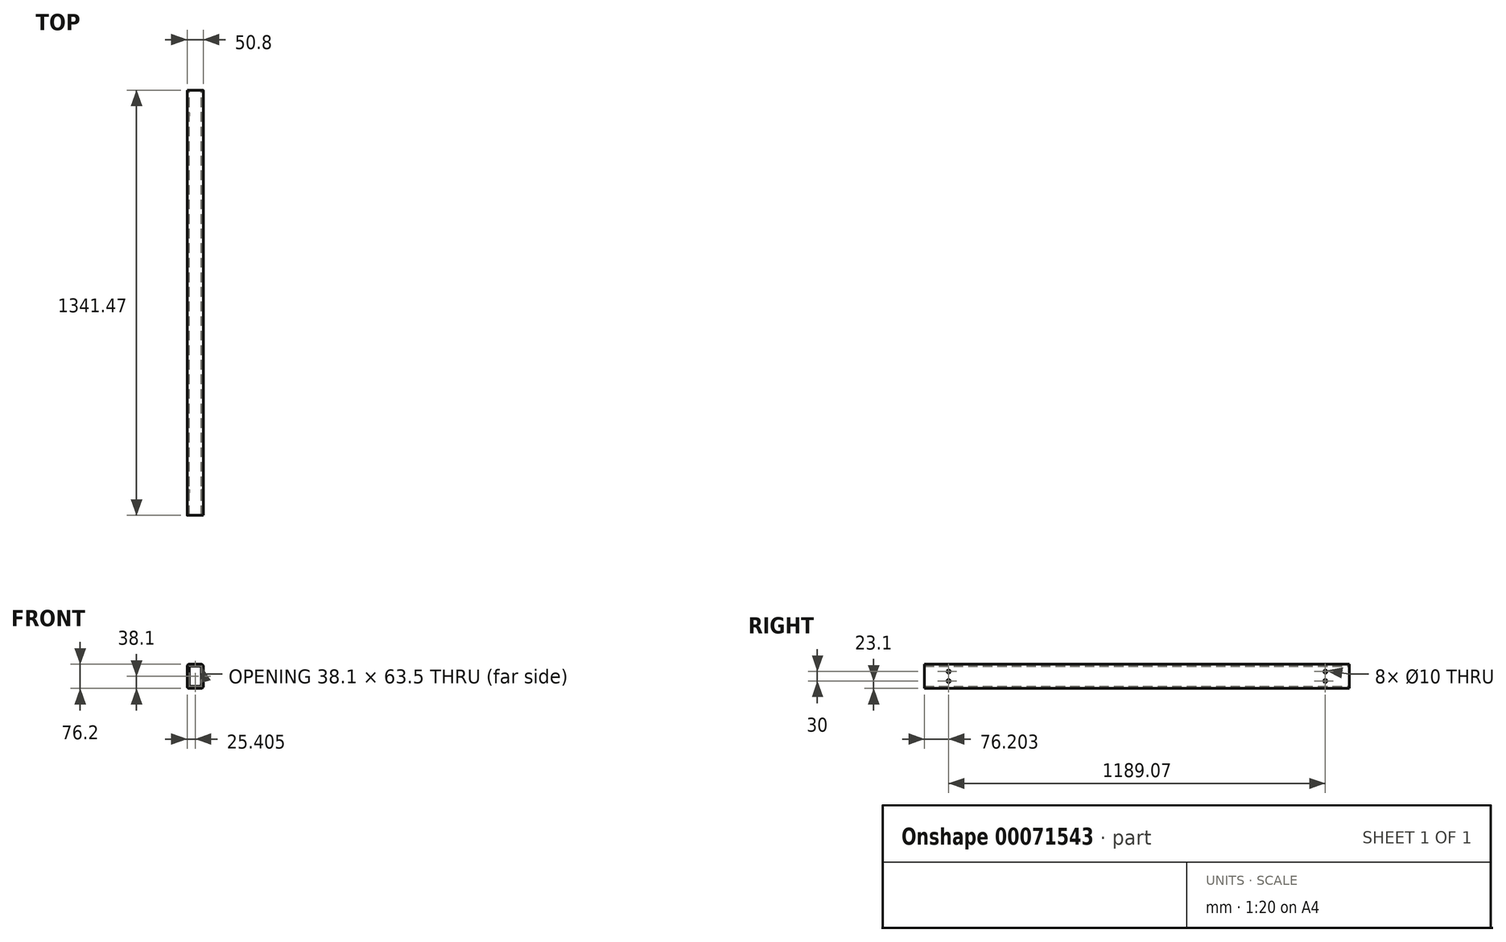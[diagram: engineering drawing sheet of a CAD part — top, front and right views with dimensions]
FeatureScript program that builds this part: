
annotation { "Feature Type Name" : "Feature", "Feature Type Description" : "" }
export const myFeature = defineFeature(function(context is Context, id is Id, definition is map)
    precondition{}
    {
        {
            var Q0;
            Q0=qCreatedBy(makeId("Front.planeOp"),FACE);
            var sketch = newSketch(context, id + "F0", { "sketchPlane" : qUnion([Q0])});
            skLineSegment(sketch, "E0.bottom", {"start": v(-40.1, 38.24) * mm, "end": v(-2, 38.24) * mm});
            skLineSegment(sketch, "E0.top", {"start": v(-40.1, -37.96) * mm, "end": v(-2, -37.96) * mm});
            skLineSegment(sketch, "E0.left", {"start": v(-46.45, 31.89) * mm, "end": v(-46.45, -31.61) * mm});
            skLineSegment(sketch, "E0.right", {"start": v(4.35, 31.89) * mm, "end": v(4.35, -31.61) * mm});
            skLineSegment(sketch, "E1.bottom", {"start": v(-33.75, 31.89) * mm, "end": v(-8.35, 31.89) * mm});
            skLineSegment(sketch, "E1.top", {"start": v(-33.75, -31.61) * mm, "end": v(-8.35, -31.61) * mm});
            skLineSegment(sketch, "E1.left", {"start": v(-40.1, 25.54) * mm, "end": v(-40.1, -25.26) * mm});
            skLineSegment(sketch, "E1.right", {"start": v(-2, 25.54) * mm, "end": v(-2, -25.26) * mm});
            skPoint(sketch, "E2.visualSharp", {"position": v(-40.1, 31.89) * mm});
            skArc(sketch, "E2.filletArc", {"start": v(-33.75, 31.89) * mm, "mid": v(-38.24, 30.03) * mm, "end": v(-40.1, 25.54) * mm});
            skPoint(sketch, "E3.visualSharp", {"position": v(-2, 31.89) * mm});
            skArc(sketch, "E3.filletArc", {"start": v(-2, 25.54) * mm, "mid": v(-3.85, 30.03) * mm, "end": v(-8.35, 31.89) * mm});
            skPoint(sketch, "E4.visualSharp", {"position": v(-2, -31.61) * mm});
            skArc(sketch, "E4.filletArc", {"start": v(-8.35, -31.61) * mm, "mid": v(-3.85, -29.75) * mm, "end": v(-2, -25.26) * mm});
            skPoint(sketch, "E5.visualSharp", {"position": v(-40.1, -31.61) * mm});
            skArc(sketch, "E5.filletArc", {"start": v(-40.1, -25.26) * mm, "mid": v(-38.24, -29.75) * mm, "end": v(-33.75, -31.61) * mm});
            skPoint(sketch, "E6.visualSharp", {"position": v(-46.45, -37.96) * mm});
            skArc(sketch, "E6.filletArc", {"start": v(-46.45, -31.61) * mm, "mid": v(-44.59, -36.1) * mm, "end": v(-40.1, -37.96) * mm});
            skPoint(sketch, "E7.visualSharp", {"position": v(4.35, -37.96) * mm});
            skArc(sketch, "E7.filletArc", {"start": v(-2, -37.96) * mm, "mid": v(2.5, -36.1) * mm, "end": v(4.35, -31.61) * mm});
            skPoint(sketch, "E8.visualSharp", {"position": v(4.35, 38.24) * mm});
            skArc(sketch, "E8.filletArc", {"start": v(4.35, 31.89) * mm, "mid": v(2.5, 36.38) * mm, "end": v(-2, 38.24) * mm});
            skPoint(sketch, "E9.visualSharp", {"position": v(-46.45, 38.24) * mm});
            skArc(sketch, "E9.filletArc", {"start": v(-40.1, 38.24) * mm, "mid": v(-44.59, 36.38) * mm, "end": v(-46.45, 31.89) * mm});
            skSolve(sketch);
        }
        {
            var Q0;
            Q0 = qSketchRegion(id + "F0", true);
            extrude(context, id + "F1", {"entities" : qUnion([Q0]), "depth" : 1341.47 * mm});
        }
        {
            var Q0;
            Q0=makeQuery(id+"F1.opExtrude","SWEPT_FACE",FACE,{"disambiguationData":[OSD([sQuery(id+"F0.wireOp",EDGE,"E0.right")])]});
            var sketch = newSketch(context, id + "F2", { "sketchPlane" : qUnion([Q0])});
            skCircle(sketch, "E10", {"center": v(-1265.27, 15.14) * mm, "radius": 5 * mm});
            skCircle(sketch, "E11", {"center": v(-1265.27, -14.86) * mm, "radius": 5 * mm});
            skCircle(sketch, "E12", {"center": v(-76.2, 15.14) * mm, "radius": 5 * mm});
            skCircle(sketch, "E13", {"center": v(-76.2, -14.86) * mm, "radius": 5 * mm});
            skSolve(sketch);
        }
        {
            var Q0;
            Q0=makeQuery(id+"F2.imprint","IMPRINT",FACE,{"disambiguationData":[TD([[makeQuery(id+"F2.imprint","IMPRINT",EDGE,{"derivedFrom":sQuery(id+"F2.wireOp",EDGE,"E12")}),1.0]])]});
            var Q1;
            Q1=makeQuery(id+"F2.imprint","IMPRINT",FACE,{"disambiguationData":[TD([[makeQuery(id+"F2.imprint","IMPRINT",EDGE,{"derivedFrom":sQuery(id+"F2.wireOp",EDGE,"E13")}),1.0]])]});
            var Q2;
            Q2=makeQuery(id+"F2.imprint","IMPRINT",FACE,{"disambiguationData":[TD([[makeQuery(id+"F2.imprint","IMPRINT",EDGE,{"derivedFrom":sQuery(id+"F2.wireOp",EDGE,"E11")}),1.0]])]});
            var Q3;
            Q3=makeQuery(id+"F2.imprint","IMPRINT",FACE,{"disambiguationData":[TD([[makeQuery(id+"F2.imprint","IMPRINT",EDGE,{"derivedFrom":sQuery(id+"F2.wireOp",EDGE,"E10")}),1.0]])]});
            extrude(context, id + "F3", {"entities" : qUnion([Q0, Q1, Q2, Q3]), "operationType" : NewBodyOperationType.REMOVE, "endBound" : BoundingType.THROUGH_ALL, "oppositeDirection" : true, "depth" : 25 * mm});
        }
    });
